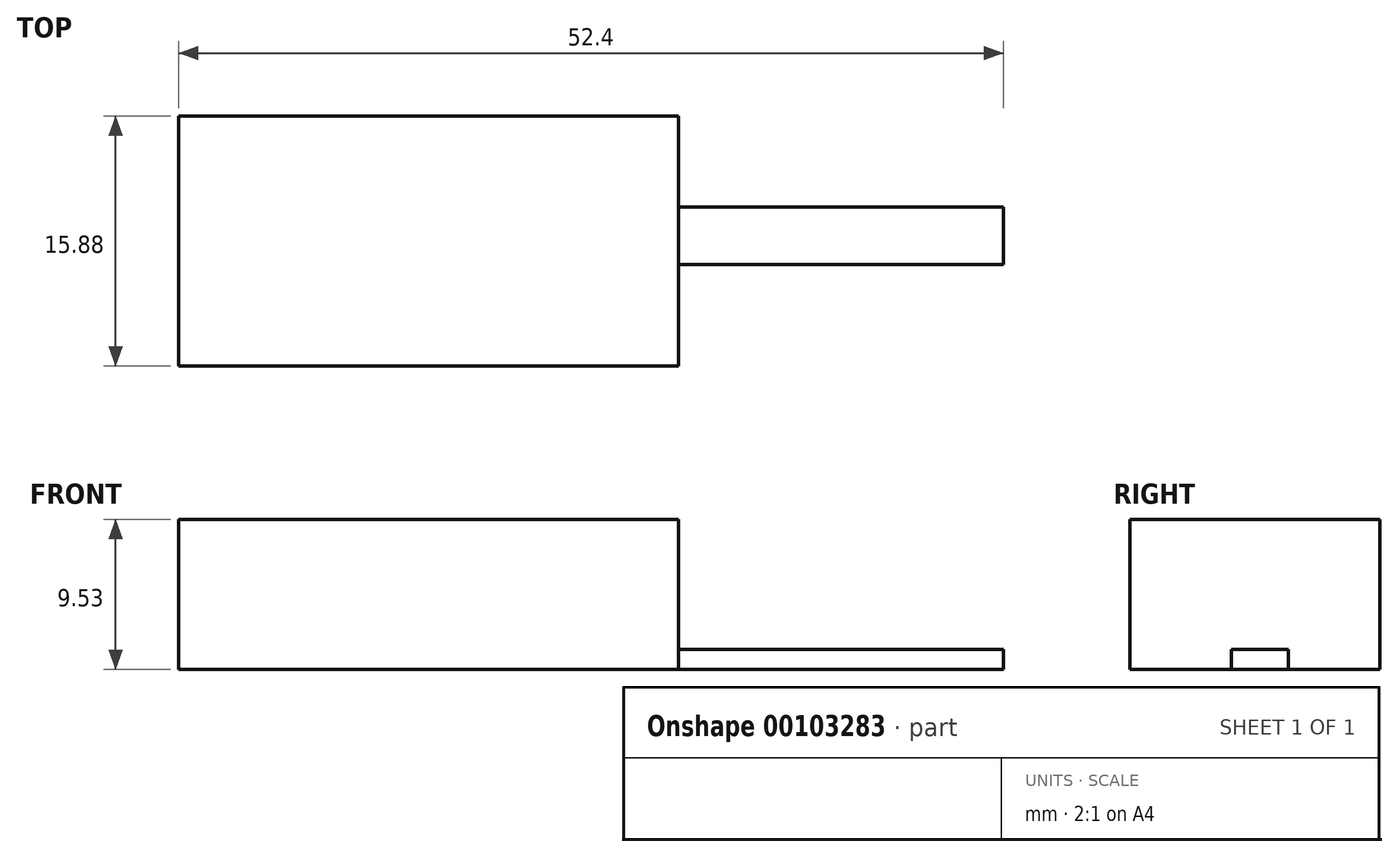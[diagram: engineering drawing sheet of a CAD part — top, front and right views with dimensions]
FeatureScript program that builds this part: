
annotation { "Feature Type Name" : "Feature", "Feature Type Description" : "" }
export const myFeature = defineFeature(function(context is Context, id is Id, definition is map)
    precondition{}
    {
        {
            var Q0;
            Q0=qCreatedBy(makeId("Front.planeOp"),FACE);
            var sketch = newSketch(context, id + "F0", { "sketchPlane" : qUnion([Q0])});
            skLineSegment(sketch, "E0.bottom", {"start": v(0, 0) * mm, "end": v(31.75, 0) * mm});
            skLineSegment(sketch, "E0.top", {"start": v(0, 9.53) * mm, "end": v(31.75, 9.53) * mm});
            skLineSegment(sketch, "E0.left", {"start": v(0, 0) * mm, "end": v(0, 9.53) * mm});
            skLineSegment(sketch, "E0.right", {"start": v(31.75, 0) * mm, "end": v(31.75, 9.53) * mm});
            skSolve(sketch);
        }
        {
            var Q0;
            Q0=makeQuery(id+"F0.imprint","IMPRINT",FACE,{"disambiguationData":[TD([[makeQuery(id+"F0.imprint","IMPRINT",EDGE,{"derivedFrom":sQuery(id+"F0.wireOp",EDGE,"E0.bottom")}),1.0]])]});
            extrude(context, id + "F1", {"entities" : qUnion([Q0]), "depth" : 15.88 * mm});
        }
        {
            var Q0;
            Q0=qCreatedBy(makeId("Top.planeOp"),FACE);
            var sketch = newSketch(context, id + "F2", { "sketchPlane" : qUnion([Q0])});
            skLineSegment(sketch, "E1.bottom", {"start": v(31.71, -5.78) * mm, "end": v(52.4, -5.78) * mm});
            skLineSegment(sketch, "E1.top", {"start": v(31.71, -9.43) * mm, "end": v(52.4, -9.43) * mm});
            skLineSegment(sketch, "E1.left", {"start": v(31.71, -5.78) * mm, "end": v(31.71, -9.43) * mm});
            skLineSegment(sketch, "E1.right", {"start": v(52.4, -5.78) * mm, "end": v(52.4, -9.43) * mm});
            skSolve(sketch);
        }
        {
            var Q0;
            Q0=makeQuery(id+"F2.imprint","IMPRINT",FACE,{"disambiguationData":[TD([[makeQuery(id+"F2.imprint","IMPRINT",EDGE,{"derivedFrom":sQuery(id+"F2.wireOp",EDGE,"E1.bottom")}),-1.0]])]});
            extrude(context, id + "F3", {"entities" : qUnion([Q0]), "operationType" : NewBodyOperationType.ADD, "depth" : 1.27 * mm});
        }
    });
